# Revit family: Door_Overhead-Sectional_WayneDalton_ThermoMark-High-Lift
name_source: partatom
category: Doors
revit_build: Autodesk Revit 2014 (Build: 20130308_1515(x64)
units: mm (PartAtom-declared; Revit-internal decimal feet)

## types (5) — shared parameters
Analytic Construction = <None>
Assembly Code = B2030410
Construction Details = http://www.wayne-dalton.com
Fire Performance = as Specified
Fire Rating = as Specified
Function = Interior
Height = 0' - 0"
Keynote = 08 36 13
Manufacturer = Wayne Dalton
Manufacturer Website = http://www.wayne-dalton.com
Operation = as Specified
Product Data = http://www.arcat.com
Product Properties = http://www.wayne-dalton.com
Revision = R1_2017-05
Rough Height = 0' - 0"
Rough Width = 0' - 0"
Sales Information = http://www.wayne-dalton.com
SpecWizard = http://www.arcat.com
Specification = http://www.arcat.com
Standards Conformance = IECC  ;  ASHRAE 90.1
Thickness = 0' - 0"
URL = http://www.wayne-dalton.com
Wall Closure = By host
Width = 0' - 0"
zero-valued in all types: Cost, Expected Lifespan (Years), Maintenance Schedule (Months), SHGC, Solar Heat Gain Coefficient, VLT, Visual Light Transmittance, Warranty Duration (Years)

## per-type parameters (varying)
| type | Air Infiltration | Description | Heat Transfer Coefficient (U) | Max Height | Max Width | Panel Thickness | Panel Type | R | STC Rating | Thermal Resistance (R) | U |
| ThermoMark 5255 | 0.07 cfm/ft^2 at 15 MPH | Wayne Dalton Insulated Overhead Sectional Door - ThermoMark 5255 as Specified | 0.1 BTU/(h·ft²·°F) | 20' - 1" | 26' - 2" | 0' - 1 7/8" | Door-Panel_Overhead-Sectional_WayneDalton_ThermoMark-5xx5 : as Specified | 16.2200 (h·ft²·°F)/BTU | 20 | 16.2200 (h·ft²·°F)/BTU | 0.1 BTU/(h·ft²·°F) |
| ThermoMark 5155 | 0.23 cfm/ft^2 at 15 MPH | Wayne Dalton Insulated Overhead Sectional Door - ThermoMark 5155 as Specified | 0.0825 BTU/(h·ft²·°F) | 20' - 1" | 20' - 2" | 0' - 1 3/8" | Door-Panel_Overhead-Sectional_WayneDalton_ThermoMark-5xx5 : as Specified | 12.1200 (h·ft²·°F)/BTU | 20 | 12.1200 (h·ft²·°F)/BTU | 0.0825 BTU/(h·ft²·°F) |
| ThermoMark 5200 | as Specified | Wayne Dalton Insulated Overhead Sectional Door - ThermoMark 5200 as Specified | 0.0616 BTU/(h·ft²·°F) | 20' - 1" | 26' - 2" | 0' - 1 7/8" | Door-Panel_Overhead-Sectional_WayneDalton_ThermoMark-5xx0 : as Specified | 16.2200 (h·ft²·°F)/BTU | 20 | 16.2200 (h·ft²·°F)/BTU | 0.0616 BTU/(h·ft²·°F) |
| ThermoMark 5150 | as Specified | Wayne Dalton Insulated Overhead Sectional Door - ThermoMark 5150 as Specified | 0.0825 BTU/(h·ft²·°F) | 20' - 1" | 20' - 2" | 0' - 1 3/8" | Door-Panel_Overhead-Sectional_WayneDalton_ThermoMark-5xx0 : as Specified | 12.1200 (h·ft²·°F)/BTU | 20 | 12.1200 (h·ft²·°F)/BTU | 0.0825 BTU/(h·ft²·°F) |
| ThermoMark 530 | 0.09 cfm/ft^2 at 15 MPH | Wayne Dalton Insulated Overhead Sectional Door - ThermoMark 530 as Specified | 0.14 BTU/(h·ft²·°F) | 24' - 1" | 40' - 2" | 0' - 3" | Door-Panel_Overhead-Sectional_WayneDalton_ThermoMark-530 : as Specified | 26.0000 (h·ft²·°F)/BTU | 22 | 26.0000 (h·ft²·°F)/BTU | 0.14 BTU/(h·ft²·°F) |

note: column(s) folded — value = type name in every type: Model

## geometry (parser evidence)
native form markers: Sweep x41
no freeform markers — native parametric forms only
